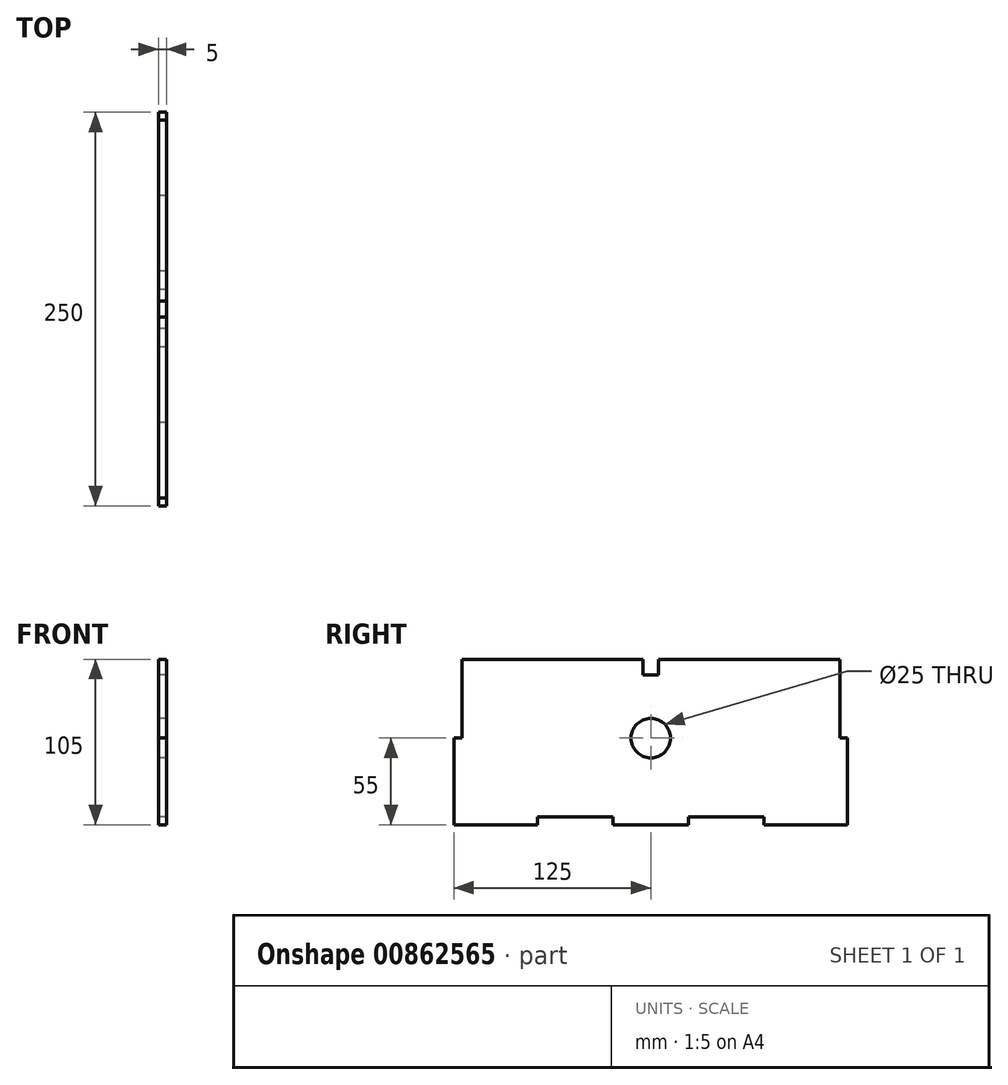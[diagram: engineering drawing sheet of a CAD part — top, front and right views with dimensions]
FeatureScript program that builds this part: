
annotation { "Feature Type Name" : "Feature", "Feature Type Description" : "" }
export const myFeature = defineFeature(function(context is Context, id is Id, definition is map)
    precondition{}
    {
        {
            var Q0;
            Q0=qCreatedBy(makeId("Right.planeOp"),FACE);
            var sketch = newSketch(context, id + "F0", { "sketchPlane" : qUnion([Q0])});
            skLineSegment(sketch, "E0.bottom", {"start": v(125, -50) * mm, "end": v(-125, -50) * mm});
            skLineSegment(sketch, "E0.top", {"start": v(125, 50) * mm, "end": v(5, 50) * mm});
            skLineSegment(sketch, "E0.left", {"start": v(125, -50) * mm, "end": v(125, 0) * mm});
            skLineSegment(sketch, "E0.right", {"start": v(-125, -50) * mm, "end": v(-125, 0) * mm});
            skPoint(sketch, "E0.middle", {"position": v(0, 0) * mm});
            skLineSegment(sketch, "E1", {"start": v(-125, -50) * mm, "end": v(-125, -55) * mm});
            skLineSegment(sketch, "E2", {"start": v(-125, -55) * mm, "end": v(-72, -55) * mm});
            skLineSegment(sketch, "E3", {"start": v(-72, -55) * mm, "end": v(-72, -50) * mm});
            skLineSegment(sketch, "E4", {"start": v(-72, -55) * mm, "end": v(-24, -55) * mm, "construction": true});
            skLineSegment(sketch, "E5", {"start": v(-24, -55) * mm, "end": v(-24, -50) * mm});
            skLineSegment(sketch, "E6", {"start": v(-24, -55) * mm, "end": v(24, -55) * mm});
            skLineSegment(sketch, "E7", {"start": v(24, -55) * mm, "end": v(24, -50) * mm});
            skLineSegment(sketch, "E8.MirrorCS", {"start": v(125, -55) * mm, "end": v(72, -55) * mm});
            skLineSegment(sketch, "E9.MirrorCS", {"start": v(72, -55) * mm, "end": v(72, -50) * mm});
            skLineSegment(sketch, "E10.MirrorCS", {"start": v(125, -50) * mm, "end": v(125, -55) * mm});
            skLineSegment(sketch, "E11", {"start": v(-120, 50) * mm, "end": v(-120, 0) * mm});
            skLineSegment(sketch, "E12", {"start": v(-120, 0) * mm, "end": v(-125, 0) * mm});
            skLineSegment(sketch, "E13.MirrorCS", {"start": v(120, 50) * mm, "end": v(120, 0) * mm});
            skLineSegment(sketch, "E14.MirrorCS", {"start": v(120, 0) * mm, "end": v(125, 0) * mm});
            skLineSegment(sketch, "E15", {"start": v(-5, 50) * mm, "end": v(-5, 40) * mm});
            skLineSegment(sketch, "E16", {"start": v(-5, 40) * mm, "end": v(0, 40) * mm});
            skLineSegment(sketch, "E17.MirrorCS", {"start": v(5, 50) * mm, "end": v(5, 40) * mm});
            skLineSegment(sketch, "E18.MirrorCS", {"start": v(5, 40) * mm, "end": v(0, 40) * mm});
            skLineSegment(sketch, "E19.trimOffspring", {"start": v(-5, 50) * mm, "end": v(-125, 50) * mm});
            skCircle(sketch, "E20", {"center": v(0, 0) * mm, "radius": 12.5 * mm});
            skSolve(sketch);
        }
        {
            var Q0;
            Q0 = qSketchRegion(id + "F0", true);
            extrude(context, id + "F1", {"entities" : qUnion([Q0]), "depth" : 5 * mm, "offsetDistance" : 25 * mm});
        }
    });
